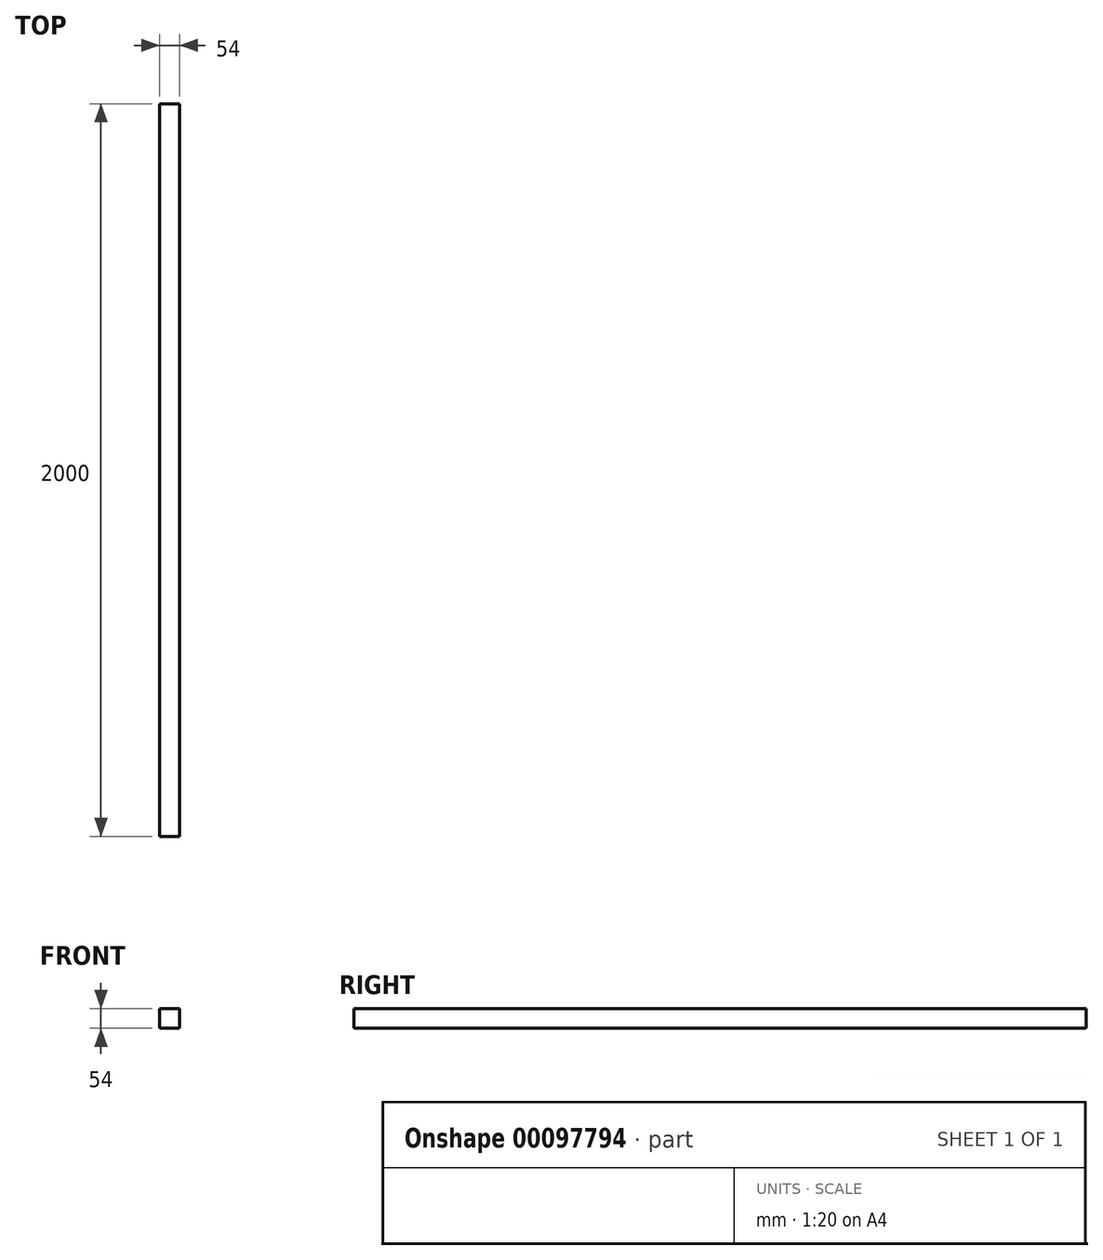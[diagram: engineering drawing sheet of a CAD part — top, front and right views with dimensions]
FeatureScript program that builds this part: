
annotation { "Feature Type Name" : "Feature", "Feature Type Description" : "" }
export const myFeature = defineFeature(function(context is Context, id is Id, definition is map)
    precondition{}
    {
        {
            var Q0;
            Q0=qCreatedBy(makeId("Front.planeOp"),FACE);
            var sketch = newSketch(context, id + "F0", { "sketchPlane" : qUnion([Q0])});
            skLineSegment(sketch, "E0.bottom", {"start": v(0, 0) * mm, "end": v(54, 0) * mm});
            skLineSegment(sketch, "E0.top", {"start": v(0, 54) * mm, "end": v(54, 54) * mm});
            skLineSegment(sketch, "E0.left", {"start": v(0, 0) * mm, "end": v(0, 54) * mm});
            skLineSegment(sketch, "E0.right", {"start": v(54, 0) * mm, "end": v(54, 54) * mm});
            skSolve(sketch);
        }
        {
            var Q0;
            Q0 = qSketchRegion(id + "F0", true);
            extrude(context, id + "F1", {"entities" : qUnion([Q0]), "oppositeDirection" : true, "depth" : 2000 * mm});
        }
    });
